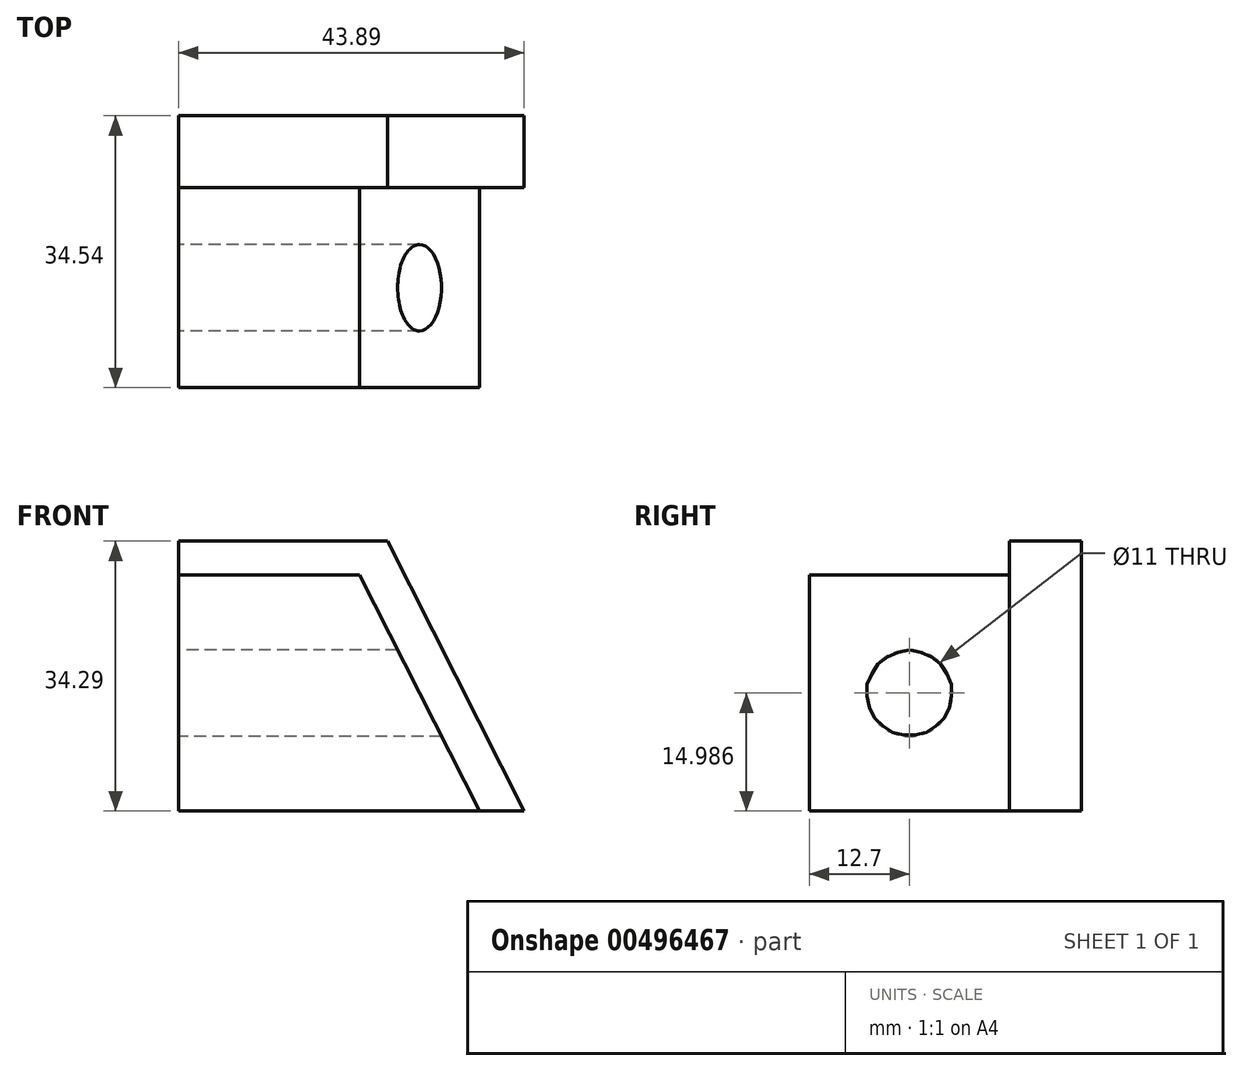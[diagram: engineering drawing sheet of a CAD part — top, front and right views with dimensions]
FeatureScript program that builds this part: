
annotation { "Feature Type Name" : "Feature", "Feature Type Description" : "" }
export const myFeature = defineFeature(function(context is Context, id is Id, definition is map)
    precondition{}
    {
        {
            var Q0;
            Q0=qCreatedBy(makeId("Front.planeOp"),FACE);
            var sketch = newSketch(context, id + "F0", { "sketchPlane" : qUnion([Q0])});
            skLineSegment(sketch, "E0", {"start": v(0, 0) * mm, "end": v(43.9, 0) * mm});
            skLineSegment(sketch, "E1", {"start": v(43.9, 0) * mm, "end": v(26.52, 34.3) * mm});
            skLineSegment(sketch, "E2", {"start": v(26.52, 34.3) * mm, "end": v(0, 34.3) * mm});
            skLineSegment(sketch, "E3", {"start": v(0, 34.3) * mm, "end": v(0, 0) * mm});
            skSolve(sketch);
        }
        {
            var Q0;
            Q0=makeQuery(id+"F0.imprint","IMPRINT",FACE,{"disambiguationData":[TD([[makeQuery(id+"F0.imprint","IMPRINT",EDGE,{"derivedFrom":sQuery(id+"F0.wireOp",EDGE,"E0")}),1.0]])]});
            extrude(context, id + "F1", {"entities" : qUnion([Q0]), "oppositeDirection" : true, "depth" : 9.14 * mm});
        }
        {
            var Q0;
            Q0=qCreatedBy(makeId("Front.planeOp"),FACE);
            var sketch = newSketch(context, id + "F2", { "sketchPlane" : qUnion([Q0])});
            skLineSegment(sketch, "E4.0", {"start": v(23.01, 29.97) * mm, "end": v(0, 29.97) * mm});
            skLineSegment(sketch, "E5.0", {"start": v(38.2, 0) * mm, "end": v(23.01, 29.97) * mm});
            skLineSegment(sketch, "E6", {"start": v(0, 29.97) * mm, "end": v(0, 0) * mm});
            skLineSegment(sketch, "E7", {"start": v(0, 0) * mm, "end": v(38.2, 0) * mm});
            skPoint(sketch, "E8.orphan", {"position": v(39.37, -2.32) * mm});
            skPoint(sketch, "E9.orphan", {"position": v(39.37, 0) * mm});
            skSolve(sketch);
        }
        {
            var Q0;
            Q0=makeQuery(id+"F2.imprint","IMPRINT",FACE,{"disambiguationData":[TD([[makeQuery(id+"F2.imprint","IMPRINT",EDGE,{"derivedFrom":sQuery(id+"F2.wireOp",EDGE,"E4.0")}),1.0]])]});
            extrude(context, id + "F3", {"entities" : qUnion([Q0]), "operationType" : NewBodyOperationType.ADD, "depth" : 25.4 * mm});
        }
        {
            var Q0;
            Q0=makeQuery(id+"F3.boolean.opBoolean","MERGE",FACE,{"derivedFrom":[makeQuery(id+"F1.opExtrude","SWEPT_FACE",FACE,{"disambiguationData":[OSD([sQuery(id+"F0.wireOp",EDGE,"E3")])]}),makeQuery(id+"F3.opExtrude","SWEPT_FACE",FACE,{"disambiguationData":[OSD([sQuery(id+"F2.wireOp",EDGE,"E6")])]})]});
            var sketch = newSketch(context, id + "F4", { "sketchPlane" : qUnion([Q0])});
            skCircle(sketch, "E10", {"center": v(12.7, 14.99) * mm, "radius": 5.5 * mm});
            skSolve(sketch);
        }
        {
            var Q0;
            Q0 = qSketchRegion(id + "F4", true);
            extrude(context, id + "F5", {"entities" : qUnion([Q0]), "operationType" : NewBodyOperationType.REMOVE, "endBound" : BoundingType.THROUGH_ALL, "oppositeDirection" : true, "depth" : 25.4 * mm});
        }
    });
